# Revit family: Storage-Teknion-CTPS_Double_Split_Combination_Tower-R2021
name_source: partatom
category: Furniture
units: mm (PartAtom-declared; Revit-internal decimal feet)

## family parameters
Always vertical = Yes
Cut with Voids When Loaded = No
OmniClass Number = 23.40.20.00
OmniClass Title = General Furniture and Specialties
Room Calculation Point = No
Shared = Yes
Work Plane-Based = No

## types (12) — shared parameters
Assembly Code = E2020200
Manufacturer = Teknion
Manufacturer Fax = 416.661.4586
Part Number = CTPS
Product Documentation Link = https://www.teknion.com
Product Line = Chronicle
Product Page URL = https://www.teknion.com
Sustainability Data = https://www.teknion.com
URL = www.teknion.com
Unit Weight URL = http://www.teknion.com
Warranty = http://www.teknion.com
zero-valued in all types: Default Elevation

## per-type parameters (varying)
| type | 2 Box Lower Configuration (Left) | 2 Box Lower Configuration (Right) | Description | File 1 Lower Configuration (Left) | File 1 Lower Configuration (Right) | File 2 Lower Configuration (Left) | File 2 Lower Configuration (Right) | Full Wardrobe | Hinged Doors Lower Configuration 1 | Hinged Doors Lower Configuration 2 | Left Split Upper | Model | Open Upper Configuration | Partial Wardrobe | Right Split Upper |
| (BF) Full Door Right, Left Upper Shelves with Box, Box, File Lower | Yes | No | Double Split Combination Tower, Full Door Right, Left Upper Shelves with Box, Box, File Lower | No | No | Yes | No | Yes | No | No | No | CTPSBF____ | Yes | No | Yes |
| (FS) Split Upper Open/Closed / File, File Lower | No | No | Double Split Combination Tower, Split Upper Open/Closed / File, File Lower | Yes | No | Yes | No | No | No | No | No | CTPSFS | Yes | Yes | Yes |
| (HS) Split Upper Open/Closed / Hinged Doors Lower | No | No | Double Split Combination Tower, Split Upper Open/Closed / Hinged Doors Lower | No | No | No | No | No | Yes | Yes | No | CTPSHS____ | Yes | Yes | Yes |
| (BS) Split Upper Open/Closed / Box, Box, File Lower | Yes | No | Double Split Combination Tower, Split Upper Open/Closed / Box, Box, File Lower | No | No | Yes | No | No | No | No | No | CTPSBS_____ | No | Yes | Yes |
| (FD) Full Door Left, Right Upper Shelves with Hinged Door Lower | No | No | Double Split Combination Tower, Full Door Left, Right Upper Shelves with Hinged Door Lower | No | No | No | No | Yes | No | Yes | Yes | CTPSFD____ | Yes | No | No |
| (SB) Split Upper Closed/Open / Box, Box, File Lower | Yes | No | Double Split Combination Tower, Split Upper Closed/Open / Box, Box, File Lower | Yes | No | Yes | No | No | No | No | Yes | CTPSSB_____ | No | Yes | No |
| (SF) Split Upper Closed/Open / File, File Lower | No | No | Double Split Combination Tower, Split Upper Closed/Open / File, File Lower | Yes | No | Yes | No | No | No | No | Yes | CTPSSF____ | Yes | Yes | No |
| (SH) Split Upper Closed/Open / Hinged Doors Lower | No | No | Double Split Combination Tower, Split Upper Closed/Open / Hinged Doors Lower | No | No | No | No | No | Yes | Yes | Yes | CTPSSH | Yes | Yes | No |
| (FB) Full Door Left, Right Upper Shelves with Box, Box, File Lower | No | Yes | Double Split Combination Tower, Full Door Left, Right Upper Shelves with Box, Box, File Lower | No | No | No | Yes | Yes | No | No | Yes | CTPSFB | No | No | No |
| (LF) Full Door Right, Left Upper Shelves with File, File Lower | No | No | Double Split Combination Tower, Full Door Right, Left Upper Shelves with File, File Lower | Yes | No | Yes | No | Yes | No | No | No | CTPSLF____ | Yes | No | Yes |
| (FL) Full Door Left, Right Upper Shelves with File, File Lower | No | No | Double Split Combination Tower, Full Door Left, Right Upper Shelves with File, File Lower | No | Yes | No | Yes | Yes | No | No | Yes | CTPSFL | Yes | No | No |
| (DF) Full Door Right, Left Upper Shelves with Hinged Door Lower | No | No | Double Split Combination Tower, Full Door Right, Left Upper Shelves with Hinged Door Lower | No | No | No | No | Yes | Yes | No | No | CTPSDF____ | Yes | No | Yes |

## geometry (parser evidence)
native form markers: Sweep x1
no freeform markers — native parametric forms only
